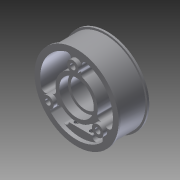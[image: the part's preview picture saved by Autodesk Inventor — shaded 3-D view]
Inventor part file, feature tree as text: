
AUTODESK INVENTOR PART (.ipt)
format: ipt  version: 2012 (Build 160160000, 160)  size: 308,224 bytes
history: native  units: in
note: dims shown in document units (in); Inventor stores cm internally (conversion verified against a paired STEP export)
features: extrude x10, thread x4, sketch x3, fillet x1
ambient origin geometry x8: Origin, YZ Plane, XZ Plane, XY Plane, X Axis, Y Axis, Z Axis, Center Point
bodies: Solid1 (feature_tree)
feature tree (18):
  sketch  "Sketch1"  dims[d0=2.75in d1=2.625in]
  extrude  "Extrusion1"  Depth=2.625in
  extrude  "Extrusion2"  Depth=0.9375in
  extrude  "Extrusion3"  Depth=0.125in
  fillet  "Fillet1"  Radius=0.1875in
  extrude  "Extrusion4"  Depth=0.6875in
  extrude  "Extrusion5"  Depth=1.1875in
  sketch  "Sketch2"  dims[d8=0.18in d10=0.9375in]
  extrude  "Extrusion8"  Depth=0.125in
  extrude  "Extrusion9"  Depth=0.1875in
  extrude  "Extrusion10"  Depth=0.9375in
  extrude  "Extrusion11"  TaperAngle=120.0deg  [1 undecoded]
  thread  "Thread1"  [1 undecoded]
  thread  "Thread2"  [1 undecoded]
  thread  "Thread3"  [1 undecoded]
  thread  "Thread4"  [1 undecoded]
  extrude  "Extrusion12"  Depth=0.9375in
  sketch  "Sketch4"  dims[d11=1.125in d12=0.125in d13=0.1875in d14=0.6875in d15=1.1875in d16=0.125in d17=0.1875in d18=0.9375in d19=120.0deg d24=1.0in d25=0.0in d26=0.9375in d27=0.0in d28=0.0625in d29=0.0in d30=0.125in d31=0.9375in d32=0.725in d33=0.0in d34=0.275in d35=0.0in d41=0.125in d42=0.0in d43=1.1811in d45=360.0deg d50=0.75in d51=0.1875in d52=0.875in d53=0.0in d54=0.125in d55=0.0in d56=0.138in d57=0.125in d58=0.125in d59=0.125in d61=0.125in d62=0.0in d63=1.0in d64=0.0in d65=1.0in d66=0.0in d67=1.0in d68=0.0in d69=1.0in d70=0.0in d72=0.125in d73=0.25in d74=0.125in d75=0.125in d76=0.125in d77=0.0in]
note: 5 required parameter values undecoded (feature->parameter linkage not recoverable at this tier; creation-order binding heuristic only, values carry confidence <= 0.55)
